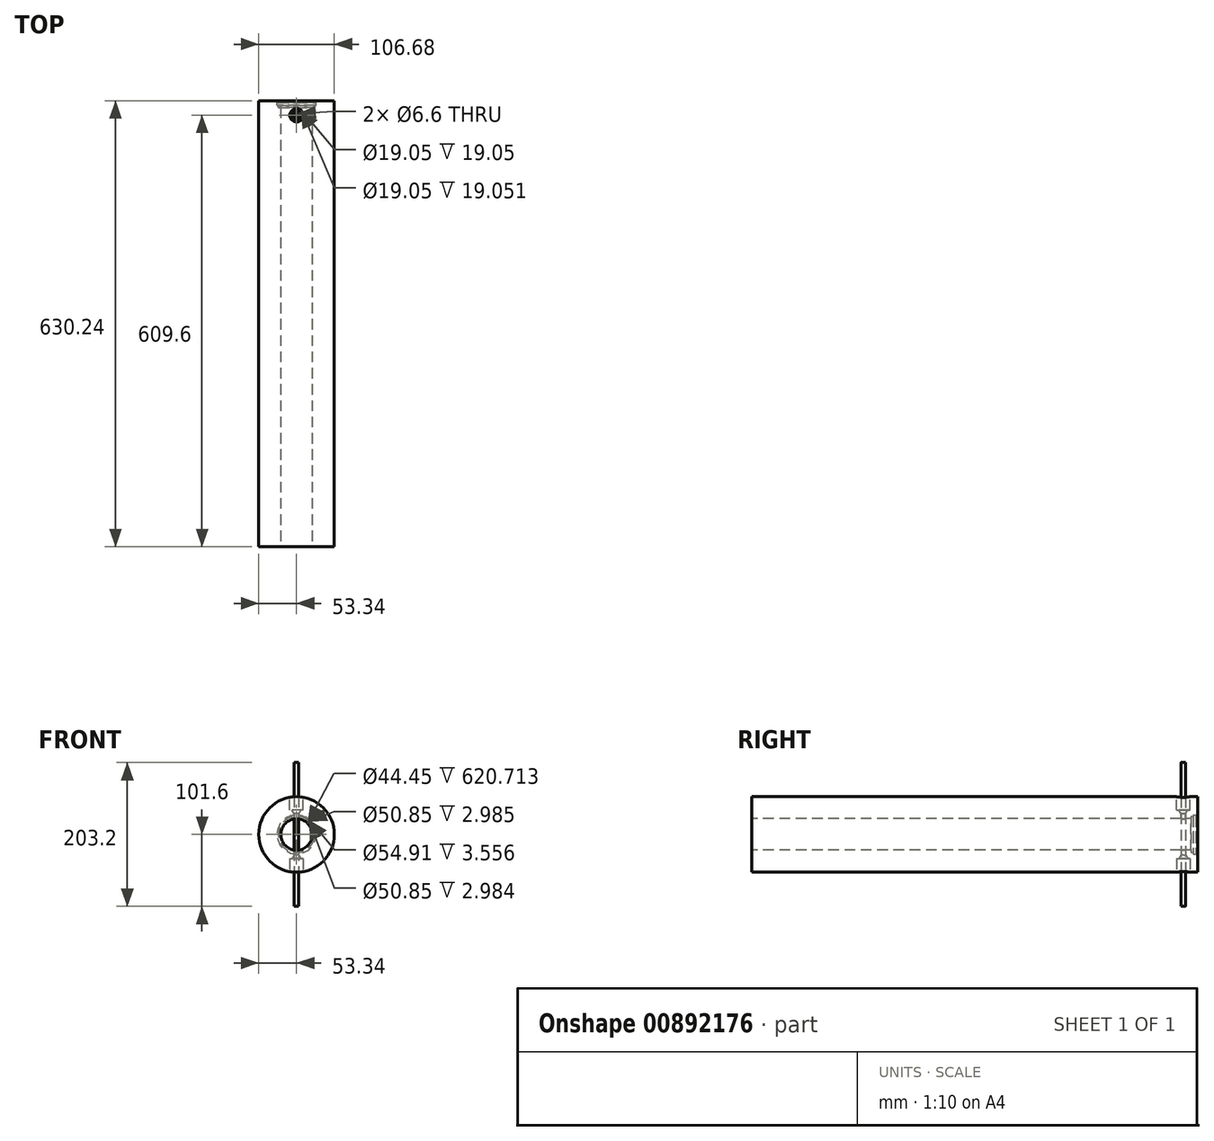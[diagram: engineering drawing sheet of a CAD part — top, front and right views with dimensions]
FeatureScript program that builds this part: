
annotation { "Feature Type Name" : "Feature", "Feature Type Description" : "" }
export const myFeature = defineFeature(function(context is Context, id is Id, definition is map)
    precondition{}
    {
        {
            var Q0;
            Q0=qCreatedBy(makeId("Front.planeOp"),FACE);
            var sketch = newSketch(context, id + "F0", { "sketchPlane" : qUnion([Q0])});
            skCircle(sketch, "E0", {"center": v(0, 0) * mm, "radius": 22.23 * mm});
            skCircle(sketch, "E1", {"center": v(0, 0) * mm, "radius": 53.34 * mm});
            skSolve(sketch);
        }
        {
            var Q0;
            Q0=makeQuery(id+"F0.imprint","IMPRINT",FACE,{"disambiguationData":[TD([[makeQuery(id+"F0.imprint","IMPRINT",EDGE,{"derivedFrom":sQuery(id+"F0.wireOp",EDGE,"E0")}),-1.0]])]});
            extrude(context, id + "F1", {"entities" : qUnion([Q0]), "oppositeDirection" : true, "depth" : 20.64 * mm, "offsetDistance" : 25.4 * mm});
        }
        {
            var Q0;
            Q0=qCreatedBy(makeId("Top.planeOp"),FACE);
            cPlane(context, id + "F2", {"entities" : qUnion([Q0]), "cplaneType" : CPlaneType.OFFSET, "offset" : 53.34 * mm, "width" : 152.4 * mm, "height" : 152.4 * mm});
        }
        {
            var Q0;
            Q0=qCreatedBy(makeId("Top.planeOp"),FACE);
            cPlane(context, id + "F3", {"entities" : qUnion([Q0]), "cplaneType" : CPlaneType.OFFSET, "offset" : 53.34 * mm, "oppositeDirection" : true, "width" : 152.4 * mm, "height" : 152.4 * mm});
        }
        {
            var Q0;
            Q0=qCreatedBy(id+"F2.planeOp",FACE);
            var sketch = newSketch(context, id + "F4", { "sketchPlane" : qUnion([Q0])});
            skCircle(sketch, "E2", {"center": v(0, 0) * mm, "radius": 9.53 * mm});
            skCircle(sketch, "E3", {"center": v(0, 0) * mm, "radius": 3.3 * mm});
            skSolve(sketch);
        }
        {
            var Q0;
            Q0=qCreatedBy(id+"F3.planeOp",FACE);
            var sketch = newSketch(context, id + "F5", { "sketchPlane" : qUnion([Q0])});
            skCircle(sketch, "E4", {"center": v(0, 0) * mm, "radius": 9.53 * mm});
            skCircle(sketch, "E5", {"center": v(0, 0) * mm, "radius": 3.3 * mm});
            skSolve(sketch);
        }
        {
            var Q0;
            Q0=makeQuery(id+"F0.imprint","IMPRINT",FACE,{"disambiguationData":[TD([[makeQuery(id+"F0.imprint","IMPRINT",EDGE,{"derivedFrom":sQuery(id+"F0.wireOp",EDGE,"E0")}),-1.0]])]});
            extrude(context, id + "F6", {"entities" : qUnion([Q0]), "operationType" : NewBodyOperationType.ADD, "depth" : 609.6 * mm, "offsetDistance" : 25.4 * mm});
        }
        {
            var Q0;
            Q0=makeQuery(id+"F5.imprint","IMPRINT",FACE,{"disambiguationData":[TD([[makeQuery(id+"F5.imprint","IMPRINT",EDGE,{"derivedFrom":sQuery(id+"F5.wireOp",EDGE,"E5")}),1.0]])]});
            var Q1;
            Q1=makeQuery(id+"F5.imprint","IMPRINT",FACE,{"disambiguationData":[TD([[makeQuery(id+"F5.imprint","IMPRINT",EDGE,{"derivedFrom":sQuery(id+"F5.wireOp",EDGE,"E4")}),1.0]])]});
            extrude(context, id + "F7", {"entities" : qUnion([Q0, Q1]), "operationType" : NewBodyOperationType.REMOVE, "depth" : 19.05 * mm, "offsetDistance" : 25.4 * mm});
        }
        {
            var Q0;
            Q0=makeQuery(id+"F5.imprint","IMPRINT",FACE,{"disambiguationData":[TD([[makeQuery(id+"F5.imprint","IMPRINT",EDGE,{"derivedFrom":sQuery(id+"F5.wireOp",EDGE,"E5")}),1.0]])]});
            var Q1;
            {var subQ0=sQuery(id+"F0.wireOp",EDGE,"E0");Q1=makeQuery(id+"F6.boolean.opBoolean","MERGE",FACE,{"derivedFrom":[makeQuery(id+"F1.opExtrude","SWEPT_FACE",FACE,{"disambiguationData":[OSD([subQ0])]}),makeQuery(id+"F6.opExtrude","SWEPT_FACE",FACE,{"disambiguationData":[OSD([subQ0])]})]});}
            extrude(context, id + "F8", {"entities" : qUnion([Q0]), "operationType" : NewBodyOperationType.REMOVE, "endBound" : BoundingType.UP_TO_SURFACE, "depth" : 25.4 * mm, "endBoundEntityFace" : qUnion([Q1]), "offsetDistance" : 25.4 * mm});
        }
        {
            var Q0;
            Q0=makeQuery(id+"F4.imprint","IMPRINT",FACE,{"disambiguationData":[TD([[makeQuery(id+"F4.imprint","IMPRINT",EDGE,{"derivedFrom":sQuery(id+"F4.wireOp",EDGE,"E2")}),1.0]])]});
            var Q1;
            Q1=makeQuery(id+"F4.imprint","IMPRINT",FACE,{"disambiguationData":[TD([[makeQuery(id+"F4.imprint","IMPRINT",EDGE,{"derivedFrom":sQuery(id+"F4.wireOp",EDGE,"E3")}),1.0]])]});
            extrude(context, id + "F9", {"entities" : qUnion([Q0, Q1]), "operationType" : NewBodyOperationType.REMOVE, "oppositeDirection" : true, "depth" : 19.05 * mm, "offsetDistance" : 25.4 * mm});
        }
        {
            var Q0;
            Q0=makeQuery(id+"F4.imprint","IMPRINT",FACE,{"disambiguationData":[TD([[makeQuery(id+"F4.imprint","IMPRINT",EDGE,{"derivedFrom":sQuery(id+"F4.wireOp",EDGE,"E3")}),1.0]])]});
            var Q1;
            {var subQ0=sQuery(id+"F0.wireOp",EDGE,"E0");Q1=makeQuery(id+"F6.boolean.opBoolean","MERGE",FACE,{"derivedFrom":[makeQuery(id+"F1.opExtrude","SWEPT_FACE",FACE,{"disambiguationData":[OSD([subQ0])]}),makeQuery(id+"F6.opExtrude","SWEPT_FACE",FACE,{"disambiguationData":[OSD([subQ0])]})]});}
            extrude(context, id + "F10", {"entities" : qUnion([Q0]), "operationType" : NewBodyOperationType.REMOVE, "endBound" : BoundingType.UP_TO_SURFACE, "oppositeDirection" : true, "depth" : 25.4 * mm, "endBoundEntityFace" : qUnion([Q1]), "offsetDistance" : 25.4 * mm});
        }
        {
            var Q0;
            Q0=qCreatedBy(makeId("Right.planeOp"),FACE);
            var sketch = newSketch(context, id + "F11", { "sketchPlane" : qUnion([Q0])});
            skLineSegment(sketch, "E6", {"start": v(0, 0) * mm, "end": v(3.3, 0) * mm});
            skLineSegment(sketch, "E7", {"start": v(3.3, 34.3) * mm, "end": v(6.35, 34.3) * mm});
            skLineSegment(sketch, "E8", {"start": v(3.3, 29.21) * mm, "end": v(6.35, 34.3) * mm});
            skLineSegment(sketch, "E9", {"start": v(3.3, -34.3) * mm, "end": v(6.35, -34.3) * mm});
            skLineSegment(sketch, "E10", {"start": v(3.3, -29.21) * mm, "end": v(6.35, -34.3) * mm});
            skLineSegment(sketch, "E11", {"start": v(0, 0) * mm, "end": v(0, 13.94) * mm});
            skLineSegment(sketch, "E12", {"start": v(0, 13.94) * mm, "end": v(0, -17.8) * mm});
            skLineSegment(sketch, "E13", {"start": v(3.3, 34.3) * mm, "end": v(3.3, 29.21) * mm});
            skLineSegment(sketch, "E14", {"start": v(3.3, -29.21) * mm, "end": v(3.3, -34.3) * mm});
            skSolve(sketch);
        }
        {
            var Q0;
            Q0 = qSketchRegion(id + "F11", true);
            var Q1;
            Q1=sQuery(id+"F11.wireOp",EDGE,"E11");
            revolve(context, id + "F12", {"operationType" : NewBodyOperationType.REMOVE, "surfaceOperationType" : NewSurfaceOperationType.NEW, "entities" : qUnion([Q0]), "axis" : qUnion([Q1]), "revolveType" : RevolveType.FULL, "oppositeDirection" : true});
        }
        {
            var Q0;
            Q0=qCreatedBy(makeId("Top.planeOp"),FACE);
            var sketch = newSketch(context, id + "F13", { "sketchPlane" : qUnion([Q0])});
            skLineSegment(sketch, "E15", {"start": v(0, 0) * mm, "end": v(0, 11.11) * mm});
            skLineSegment(sketch, "E16", {"start": v(0, 11.11) * mm, "end": v(-22.23, 11.11) * mm});
            skLineSegment(sketch, "E17", {"start": v(-22.23, 11.11) * mm, "end": v(-22.23, 20.64) * mm});
            skLineSegment(sketch, "E18", {"start": v(-22.23, 20.64) * mm, "end": v(-25.43, 20.64) * mm});
            skLineSegment(sketch, "E19", {"start": v(-25.43, 20.64) * mm, "end": v(-25.43, 11.11) * mm});
            skLineSegment(sketch, "E20", {"start": v(-25.43, 11.11) * mm, "end": v(-22.23, 11.11) * mm});
            skLineSegment(sketch, "E21", {"start": v(-27.46, 14.1) * mm, "end": v(-25.43, 14.1) * mm});
            skLineSegment(sketch, "E22", {"start": v(-27.46, 14.1) * mm, "end": v(-27.46, 17.65) * mm});
            skLineSegment(sketch, "E23", {"start": v(-27.46, 17.65) * mm, "end": v(-25.43, 17.65) * mm});
            skSolve(sketch);
        }
        {
            var Q0;
            Q0 = qSketchRegion(id + "F13", true);
            var Q1;
            Q1=sQuery(id+"F13.wireOp",EDGE,"E15");
            revolve(context, id + "F14", {"operationType" : NewBodyOperationType.REMOVE, "surfaceOperationType" : NewSurfaceOperationType.NEW, "entities" : qUnion([Q0]), "axis" : qUnion([Q1]), "revolveType" : RevolveType.FULL, "oppositeDirection" : true});
        }
        {
            var Q0;
            Q0=qCreatedBy(makeId("Top.planeOp"),FACE);
            var sketch = newSketch(context, id + "F15", { "sketchPlane" : qUnion([Q0])});
            skCircle(sketch, "E24", {"center": v(0, 0) * mm, "radius": 3.18 * mm});
            skSolve(sketch);
        }
        {
            var Q0;
            Q0=makeQuery(id+"F15.imprint","IMPRINT",FACE,{"disambiguationData":[TD([[makeQuery(id+"F15.imprint","IMPRINT",EDGE,{"derivedFrom":sQuery(id+"F15.wireOp",EDGE,"E24")}),1.0]])]});
            extrude(context, id + "F16", {"entities" : qUnion([Q0]), "endBound" : BoundingType.SYMMETRIC, "depth" : 203.2 * mm, "offsetDistance" : 25.4 * mm});
        }
        {
            var Q0;
            Q0=qCreatedBy(makeId("Top.planeOp"),FACE);
            var sketch = newSketch(context, id + "F17", { "sketchPlane" : qUnion([Q0])});
            skLineSegment(sketch, "E25", {"start": v(0, 0) * mm, "end": v(0, 18.94) * mm, "construction": true});
            skCircle(sketch, "E26", {"center": v(-25.9, 15.88) * mm, "radius": 1.52 * mm});
            skSolve(sketch);
        }
        {
            var Q0;
            Q0=sQuery(id+"F17.wireOp",EDGE,"E26");
            var Q1;
            Q1=sQuery(id+"F17.wireOp",EDGE,"E25");
            revolve(context, id + "F18", {"bodyType" : ToolBodyType.SURFACE, "surfaceOperationType" : NewSurfaceOperationType.NEW, "surfaceEntities" : qUnion([Q0]), "axis" : qUnion([Q1]), "revolveType" : RevolveType.FULL});
        }
    });
